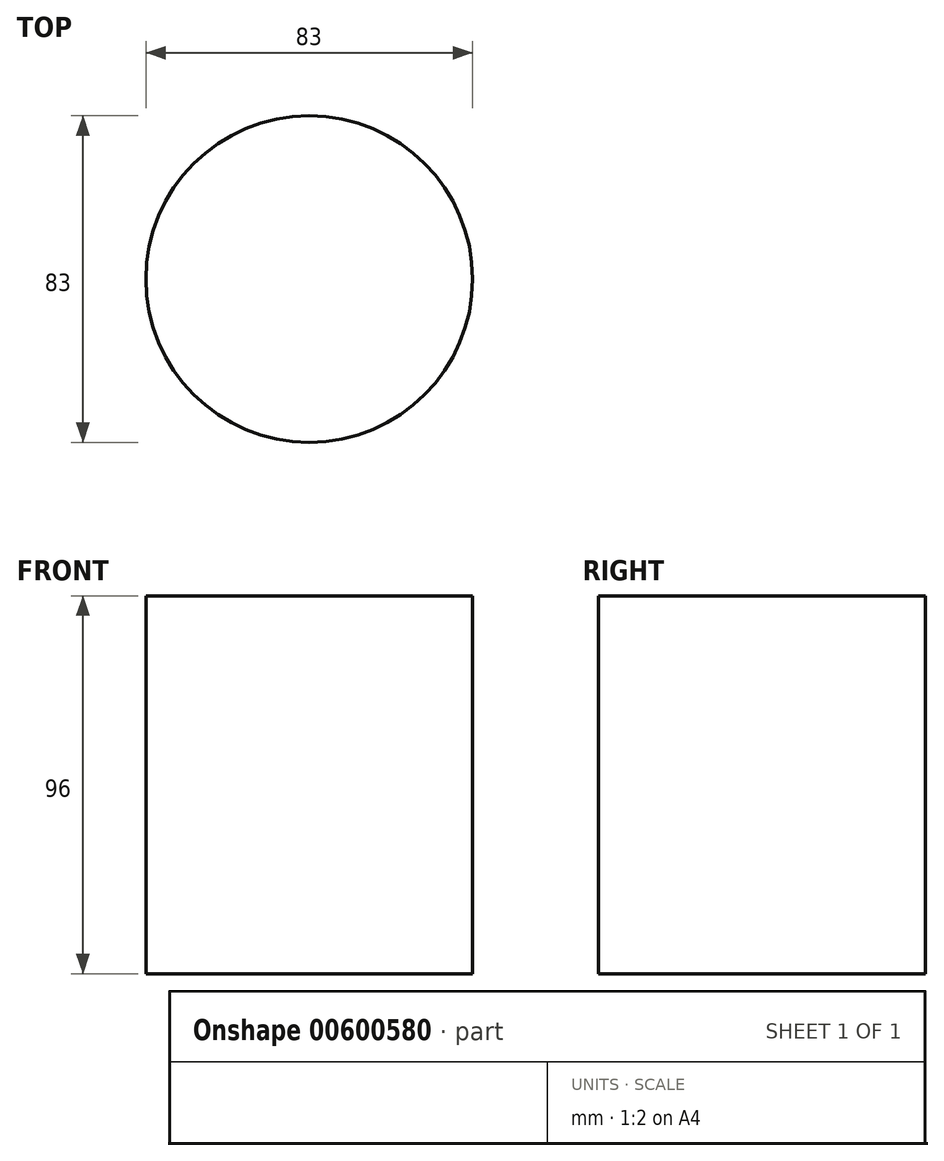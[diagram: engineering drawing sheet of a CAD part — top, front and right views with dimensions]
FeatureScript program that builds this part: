
annotation { "Feature Type Name" : "Feature", "Feature Type Description" : "" }
export const myFeature = defineFeature(function(context is Context, id is Id, definition is map)
    precondition{}
    {
        {
            var Q0;
            Q0=qCreatedBy(makeId("Top.planeOp"),FACE);
            var sketch = newSketch(context, id + "F0", { "sketchPlane" : qUnion([Q0])});
            skCircle(sketch, "E0", {"center": v(0, 0) * mm, "radius": 41.5 * mm});
            skSolve(sketch);
        }
        {
            var Q0;
            Q0 = qSketchRegion(id + "F0", true);
            extrude(context, id + "F1", {"entities" : qUnion([Q0]), "depth" : 96 * mm, "offsetDistance" : 25 * mm});
        }
    });
